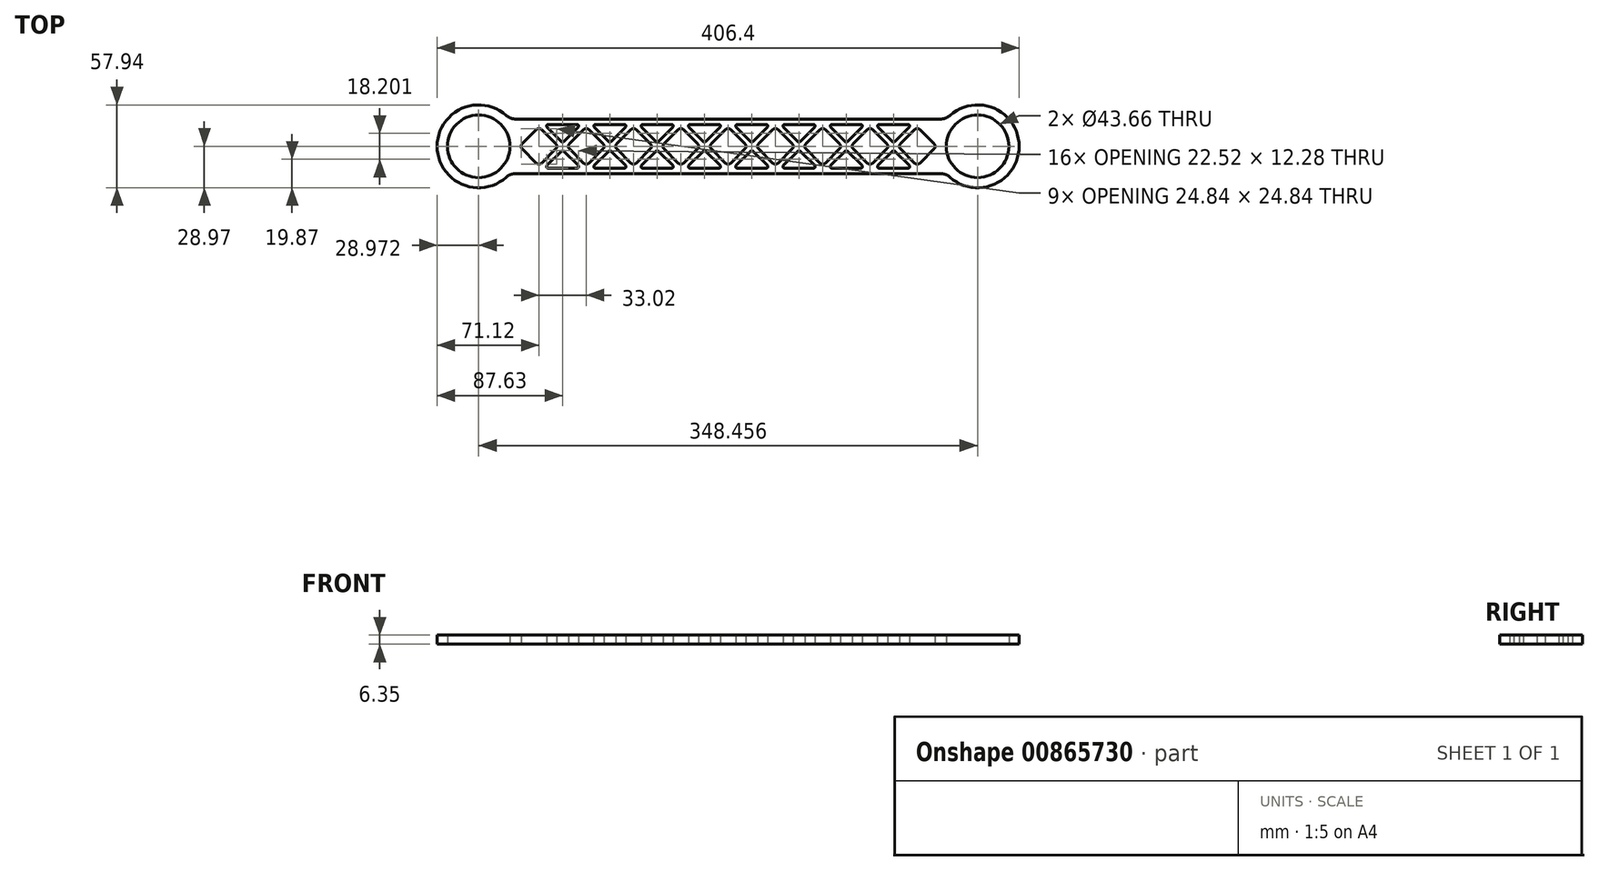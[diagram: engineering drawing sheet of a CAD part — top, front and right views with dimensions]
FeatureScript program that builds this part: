
annotation { "Feature Type Name" : "Feature", "Feature Type Description" : "" }
export const myFeature = defineFeature(function(context is Context, id is Id, definition is map)
    precondition{}
    {
        {
            var Q0;
            Q0=qCreatedBy(makeId("Top.planeOp"),FACE);
            var sketch = newSketch(context, id + "F0", { "sketchPlane" : qUnion([Q0])});
            skLineSegment(sketch, "E0.bottom", {"start": v(76.2, 9.53) * mm, "end": v(-76.2, 9.53) * mm});
            skLineSegment(sketch, "E0.top", {"start": v(76.2, -9.53) * mm, "end": v(-76.2, -9.53) * mm});
            skLineSegment(sketch, "E0.left", {"start": v(76.2, 9.53) * mm, "end": v(76.2, -9.53) * mm});
            skLineSegment(sketch, "E0.right", {"start": v(-76.2, 9.53) * mm, "end": v(-76.2, -9.53) * mm});
            skPoint(sketch, "E0.middle", {"position": v(0, 0) * mm});
            skCircle(sketch, "E1", {"center": v(-87.11, 0) * mm, "radius": 14.49 * mm});
            skPoint(sketch, "E1.third.point", {"position": v(-101.6, 0) * mm});
            skCircle(sketch, "E2", {"center": v(87.11, 0) * mm, "radius": 14.49 * mm});
            skPoint(sketch, "E2.third.point", {"position": v(101.6, 0) * mm});
            skCircle(sketch, "E3.cCircle", {"center": v(0, 0) * mm, "radius": 4.76 * mm, "construction": true});
            skLineSegment(sketch, "E3.0", {"start": v(0.9, 5.84) * mm, "end": v(5.84, 0.9) * mm});
            skLineSegment(sketch, "E3.1", {"start": v(5.84, -0.9) * mm, "end": v(0.9, -5.84) * mm});
            skLineSegment(sketch, "E3.2", {"start": v(-0.9, -5.84) * mm, "end": v(-5.84, -0.9) * mm});
            skLineSegment(sketch, "E3.3", {"start": v(-5.84, 0.9) * mm, "end": v(-0.9, 5.84) * mm});
            skPoint(sketch, "E3.0.midPoint", {"position": v(3.37, 3.37) * mm});
            skPoint(sketch, "E4", {"position": v(0, 9.53) * mm});
            skLineSegment(sketch, "E5.1.0.0", {"start": v(17.4, 5.84) * mm, "end": v(22.35, 0.9) * mm});
            skLineSegment(sketch, "E5.1.0.1", {"start": v(10.67, 0.9) * mm, "end": v(15.61, 5.84) * mm});
            skLineSegment(sketch, "E5.1.0.2", {"start": v(15.61, -5.84) * mm, "end": v(10.67, -0.9) * mm});
            skLineSegment(sketch, "E5.1.0.3", {"start": v(22.35, -0.9) * mm, "end": v(17.4, -5.84) * mm});
            skLineSegment(sketch, "E5.2.0.0", {"start": v(33.92, 5.84) * mm, "end": v(38.86, 0.9) * mm});
            skLineSegment(sketch, "E5.2.0.1", {"start": v(27.18, 0.9) * mm, "end": v(32.12, 5.84) * mm});
            skLineSegment(sketch, "E5.2.0.2", {"start": v(32.12, -5.84) * mm, "end": v(27.18, -0.9) * mm});
            skLineSegment(sketch, "E5.2.0.3", {"start": v(38.86, -0.9) * mm, "end": v(33.92, -5.84) * mm});
            skLineSegment(sketch, "E5.3.0.0", {"start": v(50.43, 5.84) * mm, "end": v(55.37, 0.9) * mm});
            skLineSegment(sketch, "E5.3.0.1", {"start": v(43.7, 0.9) * mm, "end": v(48.63, 5.84) * mm});
            skLineSegment(sketch, "E5.3.0.2", {"start": v(48.63, -5.84) * mm, "end": v(43.7, -0.9) * mm});
            skLineSegment(sketch, "E5.3.0.3", {"start": v(55.37, -0.9) * mm, "end": v(50.43, -5.84) * mm});
            skLineSegment(sketch, "E5.4.0.0", {"start": v(66.94, 5.84) * mm, "end": v(71.88, 0.9) * mm});
            skLineSegment(sketch, "E5.4.0.1", {"start": v(60.2, 0.9) * mm, "end": v(65.14, 5.84) * mm});
            skLineSegment(sketch, "E5.4.0.2", {"start": v(65.14, -5.84) * mm, "end": v(60.2, -0.9) * mm});
            skLineSegment(sketch, "E5.4.0.3", {"start": v(71.88, -0.9) * mm, "end": v(66.94, -5.84) * mm});
            skLineSegment(sketch, "E5.direction1", {"start": v(6.74, 0) * mm, "end": v(23.25, 0) * mm, "construction": true});
            skLineSegment(sketch, "E6.MirrorCS", {"start": v(-66.94, 5.84) * mm, "end": v(-71.88, 0.9) * mm});
            skLineSegment(sketch, "E7.MirrorCS", {"start": v(-60.2, 0.9) * mm, "end": v(-65.14, 5.84) * mm});
            skLineSegment(sketch, "E8.MirrorCS", {"start": v(-65.14, -5.84) * mm, "end": v(-60.2, -0.9) * mm});
            skLineSegment(sketch, "E9.MirrorCS", {"start": v(-50.43, 5.84) * mm, "end": v(-55.37, 0.9) * mm});
            skLineSegment(sketch, "E10.MirrorCS", {"start": v(-43.7, 0.9) * mm, "end": v(-48.63, 5.84) * mm});
            skLineSegment(sketch, "E11.MirrorCS", {"start": v(-48.63, -5.84) * mm, "end": v(-43.7, -0.9) * mm});
            skLineSegment(sketch, "E12.MirrorCS", {"start": v(-55.37, -0.9) * mm, "end": v(-50.43, -5.84) * mm});
            skLineSegment(sketch, "E13.MirrorCS", {"start": v(-71.88, -0.9) * mm, "end": v(-66.94, -5.84) * mm});
            skLineSegment(sketch, "E14.MirrorCS", {"start": v(-38.86, -0.9) * mm, "end": v(-33.92, -5.84) * mm});
            skLineSegment(sketch, "E15.MirrorCS", {"start": v(-33.92, 5.84) * mm, "end": v(-38.86, 0.9) * mm});
            skLineSegment(sketch, "E16.MirrorCS", {"start": v(-27.18, 0.9) * mm, "end": v(-32.12, 5.84) * mm});
            skLineSegment(sketch, "E17.MirrorCS", {"start": v(-32.12, -5.84) * mm, "end": v(-27.18, -0.9) * mm});
            skLineSegment(sketch, "E18.MirrorCS", {"start": v(-17.4, 5.84) * mm, "end": v(-22.35, 0.9) * mm});
            skLineSegment(sketch, "E19.MirrorCS", {"start": v(-10.67, 0.9) * mm, "end": v(-15.61, 5.84) * mm});
            skLineSegment(sketch, "E20.MirrorCS", {"start": v(-15.61, -5.84) * mm, "end": v(-10.67, -0.9) * mm});
            skLineSegment(sketch, "E21.MirrorCS", {"start": v(-22.35, -0.9) * mm, "end": v(-17.4, -5.84) * mm});
            skPoint(sketch, "E22.visualSharp", {"position": v(0, 6.74) * mm});
            skArc(sketch, "E22.filletArc", {"start": v(0.9, 5.84) * mm, "mid": v(0, 6.2) * mm, "end": v(-0.9, 5.84) * mm});
            skPoint(sketch, "E23.visualSharp", {"position": v(-6.74, 0) * mm});
            skArc(sketch, "E23.filletArc", {"start": v(-5.84, 0.9) * mm, "mid": v(-6.2, 0) * mm, "end": v(-5.84, -0.9) * mm});
            skPoint(sketch, "E24.visualSharp", {"position": v(0, -6.74) * mm});
            skArc(sketch, "E24.filletArc", {"start": v(-0.9, -5.84) * mm, "mid": v(0, -6.2) * mm, "end": v(0.9, -5.84) * mm});
            skPoint(sketch, "E25.visualSharp", {"position": v(6.74, 0) * mm});
            skArc(sketch, "E25.filletArc", {"start": v(5.84, -0.9) * mm, "mid": v(6.2, 0) * mm, "end": v(5.84, 0.9) * mm});
            skPoint(sketch, "E26.visualSharp", {"position": v(16.51, 6.74) * mm});
            skArc(sketch, "E26.filletArc", {"start": v(17.4, 5.84) * mm, "mid": v(16.51, 6.2) * mm, "end": v(15.61, 5.84) * mm});
            skPoint(sketch, "E27.visualSharp", {"position": v(9.77, 0) * mm});
            skArc(sketch, "E27.filletArc", {"start": v(10.67, 0.9) * mm, "mid": v(10.3, 0) * mm, "end": v(10.67, -0.9) * mm});
            skPoint(sketch, "E28.visualSharp", {"position": v(16.51, -6.74) * mm});
            skArc(sketch, "E28.filletArc", {"start": v(15.61, -5.84) * mm, "mid": v(16.51, -6.2) * mm, "end": v(17.4, -5.84) * mm});
            skPoint(sketch, "E29.visualSharp", {"position": v(23.25, 0) * mm});
            skArc(sketch, "E29.filletArc", {"start": v(22.35, -0.9) * mm, "mid": v(22.72, 0) * mm, "end": v(22.35, 0.9) * mm});
            skPoint(sketch, "E30.visualSharp", {"position": v(33.02, 6.74) * mm});
            skArc(sketch, "E30.filletArc", {"start": v(33.92, 5.84) * mm, "mid": v(33.02, 6.2) * mm, "end": v(32.12, 5.84) * mm});
            skPoint(sketch, "E31.visualSharp", {"position": v(39.76, 0) * mm});
            skArc(sketch, "E31.filletArc", {"start": v(38.86, -0.9) * mm, "mid": v(39.23, 0) * mm, "end": v(38.86, 0.9) * mm});
            skPoint(sketch, "E32.visualSharp", {"position": v(33.02, -6.74) * mm});
            skArc(sketch, "E32.filletArc", {"start": v(32.12, -5.84) * mm, "mid": v(33.02, -6.2) * mm, "end": v(33.92, -5.84) * mm});
            skPoint(sketch, "E33.visualSharp", {"position": v(26.28, 0) * mm});
            skArc(sketch, "E33.filletArc", {"start": v(27.18, 0.9) * mm, "mid": v(26.81, 0) * mm, "end": v(27.18, -0.9) * mm});
            skPoint(sketch, "E34.visualSharp", {"position": v(42.8, 0) * mm});
            skArc(sketch, "E34.filletArc", {"start": v(43.7, 0.9) * mm, "mid": v(43.32, 0) * mm, "end": v(43.7, -0.9) * mm});
            skPoint(sketch, "E35.visualSharp", {"position": v(49.53, 6.74) * mm});
            skArc(sketch, "E35.filletArc", {"start": v(50.43, 5.84) * mm, "mid": v(49.53, 6.2) * mm, "end": v(48.63, 5.84) * mm});
            skPoint(sketch, "E36.visualSharp", {"position": v(49.53, -6.74) * mm});
            skArc(sketch, "E36.filletArc", {"start": v(48.63, -5.84) * mm, "mid": v(49.53, -6.2) * mm, "end": v(50.43, -5.84) * mm});
            skPoint(sketch, "E37.visualSharp", {"position": v(56.27, 0) * mm});
            skArc(sketch, "E37.filletArc", {"start": v(55.37, -0.9) * mm, "mid": v(55.74, 0) * mm, "end": v(55.37, 0.9) * mm});
            skPoint(sketch, "E38.visualSharp", {"position": v(66.04, 6.74) * mm});
            skArc(sketch, "E38.filletArc", {"start": v(66.94, 5.84) * mm, "mid": v(66.04, 6.2) * mm, "end": v(65.14, 5.84) * mm});
            skPoint(sketch, "E39.visualSharp", {"position": v(72.78, 0) * mm});
            skArc(sketch, "E39.filletArc", {"start": v(71.88, -0.9) * mm, "mid": v(72.25, 0) * mm, "end": v(71.88, 0.9) * mm});
            skPoint(sketch, "E40.visualSharp", {"position": v(66.04, -6.74) * mm});
            skArc(sketch, "E40.filletArc", {"start": v(65.14, -5.84) * mm, "mid": v(66.04, -6.2) * mm, "end": v(66.94, -5.84) * mm});
            skPoint(sketch, "E41.visualSharp", {"position": v(59.3, 0) * mm});
            skArc(sketch, "E41.filletArc", {"start": v(60.2, 0.9) * mm, "mid": v(59.83, 0) * mm, "end": v(60.2, -0.9) * mm});
            skPoint(sketch, "E42.visualSharp", {"position": v(-9.77, 0) * mm});
            skArc(sketch, "E42.filletArc", {"start": v(-10.67, -0.9) * mm, "mid": v(-10.3, 0) * mm, "end": v(-10.67, 0.9) * mm});
            skPoint(sketch, "E43.visualSharp", {"position": v(-16.51, 6.74) * mm});
            skArc(sketch, "E43.filletArc", {"start": v(-15.61, 5.84) * mm, "mid": v(-16.51, 6.2) * mm, "end": v(-17.4, 5.84) * mm});
            skPoint(sketch, "E44.visualSharp", {"position": v(-23.25, 0) * mm});
            skArc(sketch, "E44.filletArc", {"start": v(-22.35, 0.9) * mm, "mid": v(-22.72, 0) * mm, "end": v(-22.35, -0.9) * mm});
            skPoint(sketch, "E45.visualSharp", {"position": v(-16.51, -6.74) * mm});
            skArc(sketch, "E45.filletArc", {"start": v(-17.4, -5.84) * mm, "mid": v(-16.51, -6.2) * mm, "end": v(-15.61, -5.84) * mm});
            skPoint(sketch, "E46.visualSharp", {"position": v(-33.02, -6.74) * mm});
            skArc(sketch, "E46.filletArc", {"start": v(-33.92, -5.84) * mm, "mid": v(-33.02, -6.2) * mm, "end": v(-32.12, -5.84) * mm});
            skPoint(sketch, "E47.visualSharp", {"position": v(-26.28, 0) * mm});
            skArc(sketch, "E47.filletArc", {"start": v(-27.18, -0.9) * mm, "mid": v(-26.81, 0) * mm, "end": v(-27.18, 0.9) * mm});
            skPoint(sketch, "E48.visualSharp", {"position": v(-33.02, 6.74) * mm});
            skArc(sketch, "E48.filletArc", {"start": v(-32.12, 5.84) * mm, "mid": v(-33.02, 6.2) * mm, "end": v(-33.92, 5.84) * mm});
            skPoint(sketch, "E49.visualSharp", {"position": v(-39.76, 0) * mm});
            skArc(sketch, "E49.filletArc", {"start": v(-38.86, 0.9) * mm, "mid": v(-39.23, 0) * mm, "end": v(-38.86, -0.9) * mm});
            skPoint(sketch, "E50.visualSharp", {"position": v(-49.53, 6.74) * mm});
            skArc(sketch, "E50.filletArc", {"start": v(-48.63, 5.84) * mm, "mid": v(-49.53, 6.2) * mm, "end": v(-50.43, 5.84) * mm});
            skPoint(sketch, "E51.visualSharp", {"position": v(-56.27, 0) * mm});
            skArc(sketch, "E51.filletArc", {"start": v(-55.37, 0.9) * mm, "mid": v(-55.74, 0) * mm, "end": v(-55.37, -0.9) * mm});
            skPoint(sketch, "E52.visualSharp", {"position": v(-49.53, -6.74) * mm});
            skArc(sketch, "E52.filletArc", {"start": v(-50.43, -5.84) * mm, "mid": v(-49.53, -6.2) * mm, "end": v(-48.63, -5.84) * mm});
            skPoint(sketch, "E53.visualSharp", {"position": v(-66.04, 6.74) * mm});
            skArc(sketch, "E53.filletArc", {"start": v(-65.14, 5.84) * mm, "mid": v(-66.04, 6.2) * mm, "end": v(-66.94, 5.84) * mm});
            skPoint(sketch, "E54.visualSharp", {"position": v(-72.78, 0) * mm});
            skArc(sketch, "E54.filletArc", {"start": v(-71.88, 0.9) * mm, "mid": v(-72.25, 0) * mm, "end": v(-71.88, -0.9) * mm});
            skArc(sketch, "E55.filletArc", {"start": v(-66.94, -5.84) * mm, "mid": v(-66.04, -6.2) * mm, "end": v(-65.14, -5.84) * mm});
            skPoint(sketch, "E56.visualSharp", {"position": v(-59.3, 0) * mm});
            skArc(sketch, "E56.filletArc", {"start": v(-60.2, -0.9) * mm, "mid": v(-59.83, 0) * mm, "end": v(-60.2, 0.9) * mm});
            skPoint(sketch, "E57.visualSharp", {"position": v(-42.8, 0) * mm});
            skArc(sketch, "E57.filletArc", {"start": v(-43.7, -0.9) * mm, "mid": v(-43.32, 0) * mm, "end": v(-43.7, 0.9) * mm});
            skLineSegment(sketch, "E58", {"start": v(-59.3, 0) * mm, "end": v(-56.27, 0) * mm, "construction": true});
            skLineSegment(sketch, "E59", {"start": v(-57.79, 0) * mm, "end": v(-57.79, 9.53) * mm, "construction": true});
            skLineSegment(sketch, "E60", {"start": v(-57.43, 1.63) * mm, "end": v(-52.3, 6.75) * mm});
            skLineSegment(sketch, "E61", {"start": v(-52.66, 7.62) * mm, "end": v(-62.9, 7.62) * mm});
            skLineSegment(sketch, "E62", {"start": v(-63.27, 6.75) * mm, "end": v(-58.14, 1.63) * mm});
            skPoint(sketch, "E63.visualSharp", {"position": v(-64.13, 7.62) * mm});
            skArc(sketch, "E63.filletArc", {"start": v(-62.9, 7.62) * mm, "mid": v(-63.38, 7.3) * mm, "end": v(-63.27, 6.75) * mm});
            skPoint(sketch, "E64.visualSharp", {"position": v(-51.44, 7.62) * mm});
            skArc(sketch, "E64.filletArc", {"start": v(-52.3, 6.75) * mm, "mid": v(-52.2, 7.3) * mm, "end": v(-52.66, 7.62) * mm});
            skPoint(sketch, "E65.visualSharp", {"position": v(-57.79, 1.27) * mm});
            skArc(sketch, "E65.filletArc", {"start": v(-58.14, 1.63) * mm, "mid": v(-57.79, 1.48) * mm, "end": v(-57.43, 1.63) * mm});
            skLineSegment(sketch, "E66.1.0.0", {"start": v(-40.92, 1.63) * mm, "end": v(-35.8, 6.75) * mm});
            skArc(sketch, "E66.1.0.1", {"start": v(-35.8, 6.75) * mm, "mid": v(-35.68, 7.3) * mm, "end": v(-36.15, 7.62) * mm});
            skLineSegment(sketch, "E66.1.0.2", {"start": v(-36.15, 7.62) * mm, "end": v(-46.4, 7.62) * mm});
            skArc(sketch, "E66.1.0.3", {"start": v(-41.63, 1.63) * mm, "mid": v(-41.27, 1.48) * mm, "end": v(-40.92, 1.63) * mm});
            skLineSegment(sketch, "E66.1.0.4", {"start": v(-46.76, 6.75) * mm, "end": v(-41.63, 1.63) * mm});
            skArc(sketch, "E66.1.0.5", {"start": v(-46.4, 7.62) * mm, "mid": v(-46.87, 7.3) * mm, "end": v(-46.76, 6.75) * mm});
            skLineSegment(sketch, "E66.2.0.0", {"start": v(-24.4, 1.63) * mm, "end": v(-19.28, 6.75) * mm});
            skArc(sketch, "E66.2.0.1", {"start": v(-19.28, 6.75) * mm, "mid": v(-19.17, 7.3) * mm, "end": v(-19.64, 7.62) * mm});
            skLineSegment(sketch, "E66.2.0.2", {"start": v(-19.64, 7.62) * mm, "end": v(-29.89, 7.62) * mm});
            skArc(sketch, "E66.2.0.3", {"start": v(-25.12, 1.63) * mm, "mid": v(-24.76, 1.48) * mm, "end": v(-24.4, 1.63) * mm});
            skLineSegment(sketch, "E66.2.0.4", {"start": v(-30.25, 6.75) * mm, "end": v(-25.12, 1.63) * mm});
            skArc(sketch, "E66.2.0.5", {"start": v(-29.89, 7.62) * mm, "mid": v(-30.36, 7.3) * mm, "end": v(-30.25, 6.75) * mm});
            skLineSegment(sketch, "E66.3.0.0", {"start": v(-7.9, 1.63) * mm, "end": v(-2.77, 6.75) * mm});
            skArc(sketch, "E66.3.0.1", {"start": v(-2.77, 6.75) * mm, "mid": v(-2.66, 7.3) * mm, "end": v(-3.13, 7.62) * mm});
            skLineSegment(sketch, "E66.3.0.2", {"start": v(-3.13, 7.62) * mm, "end": v(-13.38, 7.62) * mm});
            skArc(sketch, "E66.3.0.3", {"start": v(-8.61, 1.63) * mm, "mid": v(-8.25, 1.48) * mm, "end": v(-7.9, 1.63) * mm});
            skLineSegment(sketch, "E66.3.0.4", {"start": v(-13.74, 6.75) * mm, "end": v(-8.61, 1.63) * mm});
            skArc(sketch, "E66.3.0.5", {"start": v(-13.38, 7.62) * mm, "mid": v(-13.85, 7.3) * mm, "end": v(-13.74, 6.75) * mm});
            skLineSegment(sketch, "E66.4.0.0", {"start": v(8.61, 1.63) * mm, "end": v(13.74, 6.75) * mm});
            skArc(sketch, "E66.4.0.1", {"start": v(13.74, 6.75) * mm, "mid": v(13.85, 7.3) * mm, "end": v(13.38, 7.62) * mm});
            skLineSegment(sketch, "E66.4.0.2", {"start": v(13.38, 7.62) * mm, "end": v(3.13, 7.62) * mm});
            skArc(sketch, "E66.4.0.3", {"start": v(7.9, 1.63) * mm, "mid": v(8.26, 1.48) * mm, "end": v(8.61, 1.63) * mm});
            skLineSegment(sketch, "E66.4.0.4", {"start": v(2.77, 6.75) * mm, "end": v(7.9, 1.63) * mm});
            skArc(sketch, "E66.4.0.5", {"start": v(3.13, 7.62) * mm, "mid": v(2.66, 7.3) * mm, "end": v(2.77, 6.75) * mm});
            skLineSegment(sketch, "E66.5.0.0", {"start": v(25.12, 1.63) * mm, "end": v(30.25, 6.75) * mm});
            skArc(sketch, "E66.5.0.1", {"start": v(30.25, 6.75) * mm, "mid": v(30.36, 7.3) * mm, "end": v(29.89, 7.62) * mm});
            skLineSegment(sketch, "E66.5.0.2", {"start": v(29.89, 7.62) * mm, "end": v(19.64, 7.62) * mm});
            skArc(sketch, "E66.5.0.3", {"start": v(24.4, 1.63) * mm, "mid": v(24.77, 1.48) * mm, "end": v(25.12, 1.63) * mm});
            skLineSegment(sketch, "E66.5.0.4", {"start": v(19.28, 6.75) * mm, "end": v(24.4, 1.63) * mm});
            skArc(sketch, "E66.5.0.5", {"start": v(19.64, 7.62) * mm, "mid": v(19.17, 7.3) * mm, "end": v(19.28, 6.75) * mm});
            skLineSegment(sketch, "E66.6.0.0", {"start": v(41.63, 1.63) * mm, "end": v(46.76, 6.75) * mm});
            skArc(sketch, "E66.6.0.1", {"start": v(46.76, 6.75) * mm, "mid": v(46.87, 7.3) * mm, "end": v(46.4, 7.62) * mm});
            skLineSegment(sketch, "E66.6.0.2", {"start": v(46.4, 7.62) * mm, "end": v(36.15, 7.62) * mm});
            skArc(sketch, "E66.6.0.3", {"start": v(40.92, 1.63) * mm, "mid": v(41.28, 1.48) * mm, "end": v(41.63, 1.63) * mm});
            skLineSegment(sketch, "E66.6.0.4", {"start": v(35.8, 6.75) * mm, "end": v(40.92, 1.63) * mm});
            skArc(sketch, "E66.6.0.5", {"start": v(36.15, 7.62) * mm, "mid": v(35.68, 7.3) * mm, "end": v(35.8, 6.75) * mm});
            skLineSegment(sketch, "E66.7.0.0", {"start": v(58.14, 1.63) * mm, "end": v(63.27, 6.75) * mm});
            skArc(sketch, "E66.7.0.1", {"start": v(63.27, 6.75) * mm, "mid": v(63.38, 7.3) * mm, "end": v(62.9, 7.62) * mm});
            skLineSegment(sketch, "E66.7.0.2", {"start": v(62.9, 7.62) * mm, "end": v(52.66, 7.62) * mm});
            skArc(sketch, "E66.7.0.3", {"start": v(57.43, 1.63) * mm, "mid": v(57.79, 1.48) * mm, "end": v(58.14, 1.63) * mm});
            skLineSegment(sketch, "E66.7.0.4", {"start": v(52.3, 6.75) * mm, "end": v(57.43, 1.63) * mm});
            skArc(sketch, "E66.7.0.5", {"start": v(52.66, 7.62) * mm, "mid": v(52.2, 7.3) * mm, "end": v(52.3, 6.75) * mm});
            skLineSegment(sketch, "E66.direction1", {"start": v(-57.43, 1.63) * mm, "end": v(-40.92, 1.63) * mm, "construction": true});
            skLineSegment(sketch, "E67.MirrorCS", {"start": v(-63.27, -6.75) * mm, "end": v(-58.14, -1.63) * mm});
            skArc(sketch, "E68.MirrorCS", {"start": v(-62.9, -7.62) * mm, "mid": v(-63.38, -7.3) * mm, "end": v(-63.27, -6.75) * mm});
            skLineSegment(sketch, "E69.MirrorCS", {"start": v(-52.66, -7.62) * mm, "end": v(-62.9, -7.62) * mm});
            skArc(sketch, "E70.MirrorCS", {"start": v(-52.3, -6.75) * mm, "mid": v(-52.2, -7.3) * mm, "end": v(-52.66, -7.62) * mm});
            skLineSegment(sketch, "E71.MirrorCS", {"start": v(-57.43, -1.63) * mm, "end": v(-52.3, -6.75) * mm});
            skArc(sketch, "E72.MirrorCS", {"start": v(-58.14, -1.63) * mm, "mid": v(-57.79, -1.48) * mm, "end": v(-57.43, -1.63) * mm});
            skArc(sketch, "E73.MirrorCS", {"start": v(-41.63, -1.63) * mm, "mid": v(-41.27, -1.48) * mm, "end": v(-40.92, -1.63) * mm});
            skLineSegment(sketch, "E74.MirrorCS", {"start": v(-40.92, -1.63) * mm, "end": v(-35.8, -6.75) * mm});
            skLineSegment(sketch, "E75.MirrorCS", {"start": v(-46.76, -6.75) * mm, "end": v(-41.63, -1.63) * mm});
            skArc(sketch, "E76.MirrorCS", {"start": v(-46.4, -7.62) * mm, "mid": v(-46.87, -7.3) * mm, "end": v(-46.76, -6.75) * mm});
            skLineSegment(sketch, "E77.MirrorCS", {"start": v(-36.15, -7.62) * mm, "end": v(-46.4, -7.62) * mm});
            skArc(sketch, "E78.MirrorCS", {"start": v(-35.8, -6.75) * mm, "mid": v(-35.68, -7.3) * mm, "end": v(-36.15, -7.62) * mm});
            skArc(sketch, "E79.MirrorCS", {"start": v(-29.89, -7.62) * mm, "mid": v(-30.36, -7.3) * mm, "end": v(-30.25, -6.75) * mm});
            skLineSegment(sketch, "E80.MirrorCS", {"start": v(-19.64, -7.62) * mm, "end": v(-29.89, -7.62) * mm});
            skLineSegment(sketch, "E81.MirrorCS", {"start": v(-30.25, -6.75) * mm, "end": v(-25.12, -1.63) * mm});
            skLineSegment(sketch, "E82.MirrorCS", {"start": v(-24.4, -1.63) * mm, "end": v(-19.28, -6.75) * mm});
            skArc(sketch, "E83.MirrorCS", {"start": v(-19.28, -6.75) * mm, "mid": v(-19.17, -7.3) * mm, "end": v(-19.64, -7.62) * mm});
            skArc(sketch, "E84.MirrorCS", {"start": v(-25.12, -1.63) * mm, "mid": v(-24.76, -1.48) * mm, "end": v(-24.4, -1.63) * mm});
            skArc(sketch, "E85.MirrorCS", {"start": v(-8.61, -1.63) * mm, "mid": v(-8.25, -1.48) * mm, "end": v(-7.9, -1.63) * mm});
            skLineSegment(sketch, "E86.MirrorCS", {"start": v(-7.9, -1.63) * mm, "end": v(-2.77, -6.75) * mm});
            skLineSegment(sketch, "E87.MirrorCS", {"start": v(-13.74, -6.75) * mm, "end": v(-8.61, -1.63) * mm});
            skArc(sketch, "E88.MirrorCS", {"start": v(-13.38, -7.62) * mm, "mid": v(-13.85, -7.3) * mm, "end": v(-13.74, -6.75) * mm});
            skLineSegment(sketch, "E89.MirrorCS", {"start": v(-3.13, -7.62) * mm, "end": v(-13.38, -7.62) * mm});
            skArc(sketch, "E90.MirrorCS", {"start": v(-2.77, -6.75) * mm, "mid": v(-2.66, -7.3) * mm, "end": v(-3.13, -7.62) * mm});
            skArc(sketch, "E91.MirrorCS", {"start": v(3.13, -7.62) * mm, "mid": v(2.66, -7.3) * mm, "end": v(2.77, -6.75) * mm});
            skLineSegment(sketch, "E92.MirrorCS", {"start": v(13.38, -7.62) * mm, "end": v(3.13, -7.62) * mm});
            skArc(sketch, "E93.MirrorCS", {"start": v(13.74, -6.75) * mm, "mid": v(13.85, -7.3) * mm, "end": v(13.38, -7.62) * mm});
            skLineSegment(sketch, "E94.MirrorCS", {"start": v(8.61, -1.63) * mm, "end": v(13.74, -6.75) * mm});
            skArc(sketch, "E95.MirrorCS", {"start": v(7.9, -1.63) * mm, "mid": v(8.26, -1.48) * mm, "end": v(8.61, -1.63) * mm});
            skLineSegment(sketch, "E96.MirrorCS", {"start": v(2.77, -6.75) * mm, "end": v(7.9, -1.63) * mm});
            skArc(sketch, "E97.MirrorCS", {"start": v(19.64, -7.62) * mm, "mid": v(19.17, -7.3) * mm, "end": v(19.28, -6.75) * mm});
            skLineSegment(sketch, "E98.MirrorCS", {"start": v(19.28, -6.75) * mm, "end": v(24.4, -1.63) * mm});
            skLineSegment(sketch, "E99.MirrorCS", {"start": v(29.89, -7.62) * mm, "end": v(19.64, -7.62) * mm});
            skArc(sketch, "E100.MirrorCS", {"start": v(24.4, -1.63) * mm, "mid": v(24.77, -1.48) * mm, "end": v(25.12, -1.63) * mm});
            skLineSegment(sketch, "E101.MirrorCS", {"start": v(25.12, -1.63) * mm, "end": v(30.25, -6.75) * mm});
            skArc(sketch, "E102.MirrorCS", {"start": v(30.25, -6.75) * mm, "mid": v(30.36, -7.3) * mm, "end": v(29.89, -7.62) * mm});
            skArc(sketch, "E103.MirrorCS", {"start": v(36.15, -7.62) * mm, "mid": v(35.68, -7.3) * mm, "end": v(35.8, -6.75) * mm});
            skLineSegment(sketch, "E104.MirrorCS", {"start": v(46.4, -7.62) * mm, "end": v(36.15, -7.62) * mm});
            skArc(sketch, "E105.MirrorCS", {"start": v(46.76, -6.75) * mm, "mid": v(46.87, -7.3) * mm, "end": v(46.4, -7.62) * mm});
            skLineSegment(sketch, "E106.MirrorCS", {"start": v(41.63, -1.63) * mm, "end": v(46.76, -6.75) * mm});
            skArc(sketch, "E107.MirrorCS", {"start": v(40.92, -1.63) * mm, "mid": v(41.28, -1.48) * mm, "end": v(41.63, -1.63) * mm});
            skLineSegment(sketch, "E108.MirrorCS", {"start": v(35.8, -6.75) * mm, "end": v(40.92, -1.63) * mm});
            skArc(sketch, "E109.MirrorCS", {"start": v(52.66, -7.62) * mm, "mid": v(52.2, -7.3) * mm, "end": v(52.3, -6.75) * mm});
            skLineSegment(sketch, "E110.MirrorCS", {"start": v(62.9, -7.62) * mm, "end": v(52.66, -7.62) * mm});
            skArc(sketch, "E111.MirrorCS", {"start": v(63.27, -6.75) * mm, "mid": v(63.38, -7.3) * mm, "end": v(62.9, -7.62) * mm});
            skLineSegment(sketch, "E112.MirrorCS", {"start": v(58.14, -1.63) * mm, "end": v(63.27, -6.75) * mm});
            skLineSegment(sketch, "E113.MirrorCS", {"start": v(52.3, -6.75) * mm, "end": v(57.43, -1.63) * mm});
            skArc(sketch, "E114.MirrorCS", {"start": v(57.43, -1.63) * mm, "mid": v(57.79, -1.48) * mm, "end": v(58.14, -1.63) * mm});
            skCircle(sketch, "E115", {"center": v(-87.11, 0) * mm, "radius": 10.91 * mm});
            skCircle(sketch, "E116", {"center": v(87.11, 0) * mm, "radius": 10.91 * mm});
            skSolve(sketch);
        }
        {
            var Q0;
            {var subQ3=sQuery(id+"F0.wireOp",EDGE,"E115");Q0=makeQuery(id+"F0.imprint","IMPRINT",FACE,{"disambiguationData":[TD([[makeQuery(id+"F0.imprint","IMPRINT",EDGE,{"derivedFrom":subQ3}),-1.0]])]});}
            var Q1;
            {var subQ1=sQuery(id+"F0.wireOp",EDGE,"E0.right");var subQ3=makeQuery(id+"F0.imprint","INTERSECT",VERTEX,{"derivedFrom":[subQ1,sQuery(id+"F0.wireOp",EDGE,"E115")]});Q1=makeQuery(id+"F0.imprint","IMPRINT",FACE,{"disambiguationData":[TD([[makeQuery(id+"F0.imprint","IMPRINT",EDGE,{"disambiguationData":[TD([[subQ3,1.0]])],"derivedFrom":subQ1}),1.0]])]});}
            var Q2;
            {var subQ2=sQuery(id+"F0.wireOp",EDGE,"E0.bottom");Q2=makeQuery(id+"F0.imprint","IMPRINT",FACE,{"disambiguationData":[TD([[makeQuery(id+"F0.imprint","IMPRINT",EDGE,{"derivedFrom":subQ2}),1.0]])]});}
            var Q3;
            {var subQ1=sQuery(id+"F0.wireOp",EDGE,"E0.left");var subQ3=makeQuery(id+"F0.imprint","INTERSECT",VERTEX,{"derivedFrom":[subQ1,sQuery(id+"F0.wireOp",EDGE,"E116")]});Q3=makeQuery(id+"F0.imprint","IMPRINT",FACE,{"disambiguationData":[TD([[makeQuery(id+"F0.imprint","IMPRINT",EDGE,{"disambiguationData":[TD([[subQ3,1.0]])],"derivedFrom":subQ1}),-1.0]])]});}
            var Q4;
            {var subQ3=sQuery(id+"F0.wireOp",EDGE,"E116");Q4=makeQuery(id+"F0.imprint","IMPRINT",FACE,{"disambiguationData":[TD([[makeQuery(id+"F0.imprint","IMPRINT",EDGE,{"derivedFrom":subQ3}),-1.0]])]});}
            extrude(context, id + "F1", {"entities" : qUnion([Q0, Q1, Q2, Q3, Q4]), "depth" : 3.17 * mm, "offsetDistance" : 25.4 * mm});
        }
        {
            var Q0;
            Q0=makeQuery(id+"F1.opExtrude","SWEPT_EDGE",EDGE,{"disambiguationData":[OSD([sQuery(id+"F0.wireOp",EDGE,"E0.bottom"),sQuery(id+"F0.wireOp",EDGE,"E0.right"),sQuery(id+"F0.wireOp",EDGE,"E1")])]});
            var Q1;
            Q1=makeQuery(id+"F1.opExtrude","SWEPT_EDGE",EDGE,{"disambiguationData":[OSD([sQuery(id+"F0.wireOp",EDGE,"E0.top"),sQuery(id+"F0.wireOp",EDGE,"E0.right"),sQuery(id+"F0.wireOp",EDGE,"E1")])]});
            var Q2;
            Q2=makeQuery(id+"F1.opExtrude","SWEPT_EDGE",EDGE,{"disambiguationData":[OSD([sQuery(id+"F0.wireOp",EDGE,"E0.top"),sQuery(id+"F0.wireOp",EDGE,"E0.left"),sQuery(id+"F0.wireOp",EDGE,"E2")])]});
            var Q3;
            Q3=makeQuery(id+"F1.opExtrude","SWEPT_EDGE",EDGE,{"disambiguationData":[OSD([sQuery(id+"F0.wireOp",EDGE,"E0.bottom"),sQuery(id+"F0.wireOp",EDGE,"E0.left"),sQuery(id+"F0.wireOp",EDGE,"E2")])]});
            fillet(context, id + "F2", {"entities" : qUnion([Q0, Q1, Q2, Q3]), "radius" : 5.08 * mm, "tangentPropagation" : true, "allowEdgeOverflow" : false});
        }
        {
            var Q0;
            Q0=makeQuery(id+"F1.opExtrude","SWEPT_BODY",BODY,{"disambiguationData":[OSD([sQuery(id+"F0.wireOp",EDGE,"E0.bottom"),sQuery(id+"F0.wireOp",EDGE,"E0.top"),sQuery(id+"F0.wireOp",EDGE,"E1"),sQuery(id+"F0.wireOp",EDGE,"E2"),sQuery(id+"F0.wireOp",EDGE,"E3.0"),sQuery(id+"F0.wireOp",EDGE,"E3.1"),sQuery(id+"F0.wireOp",EDGE,"E3.2"),sQuery(id+"F0.wireOp",EDGE,"E3.3"),sQuery(id+"F0.wireOp",EDGE,"E5.1.0.0"),sQuery(id+"F0.wireOp",EDGE,"E5.1.0.1"),sQuery(id+"F0.wireOp",EDGE,"E5.1.0.2"),sQuery(id+"F0.wireOp",EDGE,"E5.1.0.3"),sQuery(id+"F0.wireOp",EDGE,"E5.2.0.0"),sQuery(id+"F0.wireOp",EDGE,"E5.2.0.1"),sQuery(id+"F0.wireOp",EDGE,"E5.2.0.2"),sQuery(id+"F0.wireOp",EDGE,"E5.2.0.3"),sQuery(id+"F0.wireOp",EDGE,"E5.3.0.0"),sQuery(id+"F0.wireOp",EDGE,"E5.3.0.1"),sQuery(id+"F0.wireOp",EDGE,"E5.3.0.2"),sQuery(id+"F0.wireOp",EDGE,"E5.3.0.3"),sQuery(id+"F0.wireOp",EDGE,"E5.4.0.0"),sQuery(id+"F0.wireOp",EDGE,"E5.4.0.1"),sQuery(id+"F0.wireOp",EDGE,"E5.4.0.2"),sQuery(id+"F0.wireOp",EDGE,"E5.4.0.3"),sQuery(id+"F0.wireOp",EDGE,"E6.MirrorCS"),sQuery(id+"F0.wireOp",EDGE,"E7.MirrorCS"),sQuery(id+"F0.wireOp",EDGE,"E8.MirrorCS"),sQuery(id+"F0.wireOp",EDGE,"E9.MirrorCS"),sQuery(id+"F0.wireOp",EDGE,"E10.MirrorCS"),sQuery(id+"F0.wireOp",EDGE,"E11.MirrorCS"),sQuery(id+"F0.wireOp",EDGE,"E12.MirrorCS"),sQuery(id+"F0.wireOp",EDGE,"E13.MirrorCS"),sQuery(id+"F0.wireOp",EDGE,"E14.MirrorCS"),sQuery(id+"F0.wireOp",EDGE,"E15.MirrorCS"),sQuery(id+"F0.wireOp",EDGE,"E16.MirrorCS"),sQuery(id+"F0.wireOp",EDGE,"E17.MirrorCS"),sQuery(id+"F0.wireOp",EDGE,"E18.MirrorCS"),sQuery(id+"F0.wireOp",EDGE,"E19.MirrorCS"),sQuery(id+"F0.wireOp",EDGE,"E20.MirrorCS"),sQuery(id+"F0.wireOp",EDGE,"E21.MirrorCS"),sQuery(id+"F0.wireOp",EDGE,"E22.filletArc"),sQuery(id+"F0.wireOp",EDGE,"E23.filletArc"),sQuery(id+"F0.wireOp",EDGE,"E24.filletArc"),sQuery(id+"F0.wireOp",EDGE,"E25.filletArc"),sQuery(id+"F0.wireOp",EDGE,"E26.filletArc"),sQuery(id+"F0.wireOp",EDGE,"E27.filletArc"),sQuery(id+"F0.wireOp",EDGE,"E28.filletArc"),sQuery(id+"F0.wireOp",EDGE,"E29.filletArc"),sQuery(id+"F0.wireOp",EDGE,"E30.filletArc"),sQuery(id+"F0.wireOp",EDGE,"E31.filletArc"),sQuery(id+"F0.wireOp",EDGE,"E32.filletArc"),sQuery(id+"F0.wireOp",EDGE,"E33.filletArc"),sQuery(id+"F0.wireOp",EDGE,"E34.filletArc"),sQuery(id+"F0.wireOp",EDGE,"E35.filletArc"),sQuery(id+"F0.wireOp",EDGE,"E36.filletArc"),sQuery(id+"F0.wireOp",EDGE,"E37.filletArc"),sQuery(id+"F0.wireOp",EDGE,"E38.filletArc"),sQuery(id+"F0.wireOp",EDGE,"E39.filletArc"),sQuery(id+"F0.wireOp",EDGE,"E40.filletArc"),sQuery(id+"F0.wireOp",EDGE,"E41.filletArc"),sQuery(id+"F0.wireOp",EDGE,"E42.filletArc"),sQuery(id+"F0.wireOp",EDGE,"E43.filletArc"),sQuery(id+"F0.wireOp",EDGE,"E44.filletArc"),sQuery(id+"F0.wireOp",EDGE,"E45.filletArc"),sQuery(id+"F0.wireOp",EDGE,"E46.filletArc"),sQuery(id+"F0.wireOp",EDGE,"E47.filletArc"),sQuery(id+"F0.wireOp",EDGE,"E48.filletArc"),sQuery(id+"F0.wireOp",EDGE,"E49.filletArc"),sQuery(id+"F0.wireOp",EDGE,"E50.filletArc"),sQuery(id+"F0.wireOp",EDGE,"E51.filletArc"),sQuery(id+"F0.wireOp",EDGE,"E52.filletArc"),sQuery(id+"F0.wireOp",EDGE,"E53.filletArc"),sQuery(id+"F0.wireOp",EDGE,"E54.filletArc"),sQuery(id+"F0.wireOp",EDGE,"E55.filletArc"),sQuery(id+"F0.wireOp",EDGE,"E56.filletArc"),sQuery(id+"F0.wireOp",EDGE,"E57.filletArc"),sQuery(id+"F0.wireOp",EDGE,"E60"),sQuery(id+"F0.wireOp",EDGE,"E61"),sQuery(id+"F0.wireOp",EDGE,"E62"),sQuery(id+"F0.wireOp",EDGE,"E63.filletArc"),sQuery(id+"F0.wireOp",EDGE,"E64.filletArc"),sQuery(id+"F0.wireOp",EDGE,"E65.filletArc"),sQuery(id+"F0.wireOp",EDGE,"E66.1.0.0"),sQuery(id+"F0.wireOp",EDGE,"E66.1.0.1"),sQuery(id+"F0.wireOp",EDGE,"E66.1.0.2"),sQuery(id+"F0.wireOp",EDGE,"E66.1.0.3"),sQuery(id+"F0.wireOp",EDGE,"E66.1.0.4"),sQuery(id+"F0.wireOp",EDGE,"E66.1.0.5"),sQuery(id+"F0.wireOp",EDGE,"E66.2.0.0"),sQuery(id+"F0.wireOp",EDGE,"E66.2.0.1"),sQuery(id+"F0.wireOp",EDGE,"E66.2.0.2"),sQuery(id+"F0.wireOp",EDGE,"E66.2.0.3"),sQuery(id+"F0.wireOp",EDGE,"E66.2.0.4"),sQuery(id+"F0.wireOp",EDGE,"E66.2.0.5"),sQuery(id+"F0.wireOp",EDGE,"E66.3.0.0"),sQuery(id+"F0.wireOp",EDGE,"E66.3.0.1"),sQuery(id+"F0.wireOp",EDGE,"E66.3.0.2"),sQuery(id+"F0.wireOp",EDGE,"E66.3.0.3"),sQuery(id+"F0.wireOp",EDGE,"E66.3.0.4"),sQuery(id+"F0.wireOp",EDGE,"E66.3.0.5"),sQuery(id+"F0.wireOp",EDGE,"E66.4.0.0"),sQuery(id+"F0.wireOp",EDGE,"E66.4.0.1"),sQuery(id+"F0.wireOp",EDGE,"E66.4.0.2"),sQuery(id+"F0.wireOp",EDGE,"E66.4.0.3"),sQuery(id+"F0.wireOp",EDGE,"E66.4.0.4"),sQuery(id+"F0.wireOp",EDGE,"E66.4.0.5"),sQuery(id+"F0.wireOp",EDGE,"E66.5.0.0"),sQuery(id+"F0.wireOp",EDGE,"E66.5.0.1"),sQuery(id+"F0.wireOp",EDGE,"E66.5.0.2"),sQuery(id+"F0.wireOp",EDGE,"E66.5.0.3"),sQuery(id+"F0.wireOp",EDGE,"E66.5.0.4"),sQuery(id+"F0.wireOp",EDGE,"E66.5.0.5"),sQuery(id+"F0.wireOp",EDGE,"E66.6.0.0"),sQuery(id+"F0.wireOp",EDGE,"E66.6.0.1"),sQuery(id+"F0.wireOp",EDGE,"E66.6.0.2"),sQuery(id+"F0.wireOp",EDGE,"E66.6.0.3"),sQuery(id+"F0.wireOp",EDGE,"E66.6.0.4"),sQuery(id+"F0.wireOp",EDGE,"E66.6.0.5"),sQuery(id+"F0.wireOp",EDGE,"E66.7.0.0"),sQuery(id+"F0.wireOp",EDGE,"E66.7.0.1"),sQuery(id+"F0.wireOp",EDGE,"E66.7.0.2"),sQuery(id+"F0.wireOp",EDGE,"E66.7.0.3"),sQuery(id+"F0.wireOp",EDGE,"E66.7.0.4"),sQuery(id+"F0.wireOp",EDGE,"E66.7.0.5"),sQuery(id+"F0.wireOp",EDGE,"E67.MirrorCS"),sQuery(id+"F0.wireOp",EDGE,"E68.MirrorCS"),sQuery(id+"F0.wireOp",EDGE,"E69.MirrorCS"),sQuery(id+"F0.wireOp",EDGE,"E70.MirrorCS"),sQuery(id+"F0.wireOp",EDGE,"E71.MirrorCS"),sQuery(id+"F0.wireOp",EDGE,"E72.MirrorCS"),sQuery(id+"F0.wireOp",EDGE,"E73.MirrorCS"),sQuery(id+"F0.wireOp",EDGE,"E74.MirrorCS"),sQuery(id+"F0.wireOp",EDGE,"E75.MirrorCS"),sQuery(id+"F0.wireOp",EDGE,"E76.MirrorCS"),sQuery(id+"F0.wireOp",EDGE,"E77.MirrorCS"),sQuery(id+"F0.wireOp",EDGE,"E78.MirrorCS"),sQuery(id+"F0.wireOp",EDGE,"E79.MirrorCS"),sQuery(id+"F0.wireOp",EDGE,"E80.MirrorCS"),sQuery(id+"F0.wireOp",EDGE,"E81.MirrorCS"),sQuery(id+"F0.wireOp",EDGE,"E82.MirrorCS"),sQuery(id+"F0.wireOp",EDGE,"E83.MirrorCS"),sQuery(id+"F0.wireOp",EDGE,"E84.MirrorCS"),sQuery(id+"F0.wireOp",EDGE,"E85.MirrorCS"),sQuery(id+"F0.wireOp",EDGE,"E86.MirrorCS"),sQuery(id+"F0.wireOp",EDGE,"E87.MirrorCS"),sQuery(id+"F0.wireOp",EDGE,"E88.MirrorCS"),sQuery(id+"F0.wireOp",EDGE,"E89.MirrorCS"),sQuery(id+"F0.wireOp",EDGE,"E90.MirrorCS"),sQuery(id+"F0.wireOp",EDGE,"E91.MirrorCS"),sQuery(id+"F0.wireOp",EDGE,"E92.MirrorCS"),sQuery(id+"F0.wireOp",EDGE,"E93.MirrorCS"),sQuery(id+"F0.wireOp",EDGE,"E94.MirrorCS"),sQuery(id+"F0.wireOp",EDGE,"E95.MirrorCS"),sQuery(id+"F0.wireOp",EDGE,"E96.MirrorCS"),sQuery(id+"F0.wireOp",EDGE,"E97.MirrorCS"),sQuery(id+"F0.wireOp",EDGE,"E98.MirrorCS"),sQuery(id+"F0.wireOp",EDGE,"E99.MirrorCS"),sQuery(id+"F0.wireOp",EDGE,"E100.MirrorCS"),sQuery(id+"F0.wireOp",EDGE,"E101.MirrorCS"),sQuery(id+"F0.wireOp",EDGE,"E102.MirrorCS"),sQuery(id+"F0.wireOp",EDGE,"E103.MirrorCS"),sQuery(id+"F0.wireOp",EDGE,"E104.MirrorCS"),sQuery(id+"F0.wireOp",EDGE,"E105.MirrorCS"),sQuery(id+"F0.wireOp",EDGE,"E106.MirrorCS"),sQuery(id+"F0.wireOp",EDGE,"E107.MirrorCS"),sQuery(id+"F0.wireOp",EDGE,"E108.MirrorCS"),sQuery(id+"F0.wireOp",EDGE,"E109.MirrorCS"),sQuery(id+"F0.wireOp",EDGE,"E110.MirrorCS"),sQuery(id+"F0.wireOp",EDGE,"E111.MirrorCS"),sQuery(id+"F0.wireOp",EDGE,"E112.MirrorCS"),sQuery(id+"F0.wireOp",EDGE,"E113.MirrorCS"),sQuery(id+"F0.wireOp",EDGE,"E114.MirrorCS"),sQuery(id+"F0.wireOp",EDGE,"E115"),sQuery(id+"F0.wireOp",EDGE,"E116")])]});
            var Q1;
            Q1=qCreatedBy(makeId("Origin.pointOp"),VERTEX);
            transform(context, id + "F3", {"entities" : qUnion([Q0]), "transformType" : TransformType.SCALE_UNIFORMLY, "scale" : 2, "scalePoint" : qUnion([Q1]), "makeCopy" : false});
        }
    });
